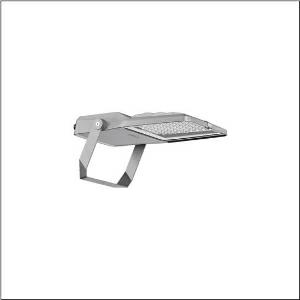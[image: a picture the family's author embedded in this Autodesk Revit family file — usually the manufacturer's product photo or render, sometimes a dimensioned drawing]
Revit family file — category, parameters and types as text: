
# Revit family: floodlight_fl_21_mini___pl64_5xa7772c4e1a_1432
name_source: partatom
category: Lighting Fixtures
units: mm (PartAtom-declared; Revit-internal decimal feet)

## family parameters
Cut with Voids When Loaded = No
Host = Face
Light Source = No
Part Type = Normal
Room Calculation Point = No
Round Connector Dimension = Use Diameter
Shared = No

## types (1)
- --- (1 x LED, 12280 lm, 87.2 W, 4000K)
    Apparent Load = 87 VA
    CIE Flux Codes = 28 80 98 100 100
    Color Rendering = 70
    Color Temperature = 4000K
    Default Elevation = 1800 mm
    Description = Floodlight FL 21 mini, floodlight, primary light control with lens, of PMMA, primary optical cover: protective disc, of toughened safety glass, transparent, light distribution: PL64, light emission: direct distribution, installation type: surface-mounted, LED, High Power LED, rated luminous flux: 12.280lm, luminous efficacy: 141lm/W, light colour: 740, colour temperature: 4000K, control gear: ECG iQ, control: Street-Remote, Auto-Match, Temp-Guard, Night-Set, Smart-Wire, Desk-Remote (wireless, voltage-free reading and setting of iQ features in the workshop via application-optimized NFC function/RFID function), optimised constant luminous flux control (CLO 2.0), with terminal, 6-pole, mains connection: 220..240V, AC, 50/60Hz, start of lifetime: 87W, end of lifetime: 92W, reduction: 40W, luminaire housing, of diecast aluminium, powder-coated, Siteco® metallic grey (DB 702S), corrosivity category C5 according to DIN EN ISO 12944, mounting bracket, of steel, galvanised, powder-coated, Siteco® metallic grey (DB 702S), protection rating (complete): IP66, insulation class (complete): insulation class II (safety insulation), certification: CE, ENEC, VDE, protection symbol: D, impact resistance: IK08, permissible operating ambient temperature: -40..+40°C, permissible operating ambient temperature for outdoor applications: -40..+50°C, standard: DIN EN 12944, packaging unit: 1 piece

Light Distribution: PL64
    Height = 70 mm
    Lamp = 1 x LED
    Lamp Light Flux = 12280 lm
    Lamp Power = 87.2 W
    Lamp count = 1
    Length = 485 mm
    Luminous efficacy = 141 lm/W
    Manufacturer = Siteco
    ModVariant = No
    Model = 5XA7772C4E1A
    Number of Poles = 1
    OnlyDefault = Yes
    Power Factor = 1
    Product Name = Floodlight FL 21 mini | PL64
    Product group = floodlight | pylon top
    ProductGroupID = 6101
    Protection Class = Protection class II
    Protection Degree = IP 66
    RLX_Detail_Level = 1
    RlxData = <blob elided: 96189 chars, md5=3c8b5acf>
    Socket = socket
    Standby Power = 0 W
    System Light Flux = 12280 lm
    System Power = 87 W
    Type Comments = factory setting: luminous flux: 100 % | dim-lin: 254 | 456 mA
    Type Image = l_1006845.jpg
    URL = http://relux.com
    VarID = @adj_077341
    Voltage = 0 V
    Weight = 0.00 kg
    Width = 337 mm

## geometry (parser evidence)
native form markers: Blend x4, Sweep x12
no freeform markers — native parametric forms only
